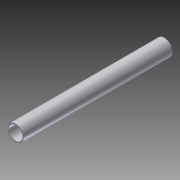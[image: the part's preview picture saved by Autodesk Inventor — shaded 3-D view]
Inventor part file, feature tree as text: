
AUTODESK INVENTOR PART (.ipt)
format: ipt  version: 2013 (Build 170138000, 138)  size: 73,216 bytes
history: native  units: in
note: dims shown in document units (in); Inventor stores cm internally (conversion verified against a paired STEP export)
features: extrude x1, sketch x1
ambient origin geometry x8: Origin, YZ Plane, XZ Plane, XY Plane, X Axis, Y Axis, Z Axis, Center Point
bodies: Solid1 (feature_tree)
feature tree (2):
  extrude  "Extrusion1"  Depth=2.0in
  sketch  "Sketch1"  dims[d0=2.375in d2=2.0in d3=21.75in d4=0.0in]
